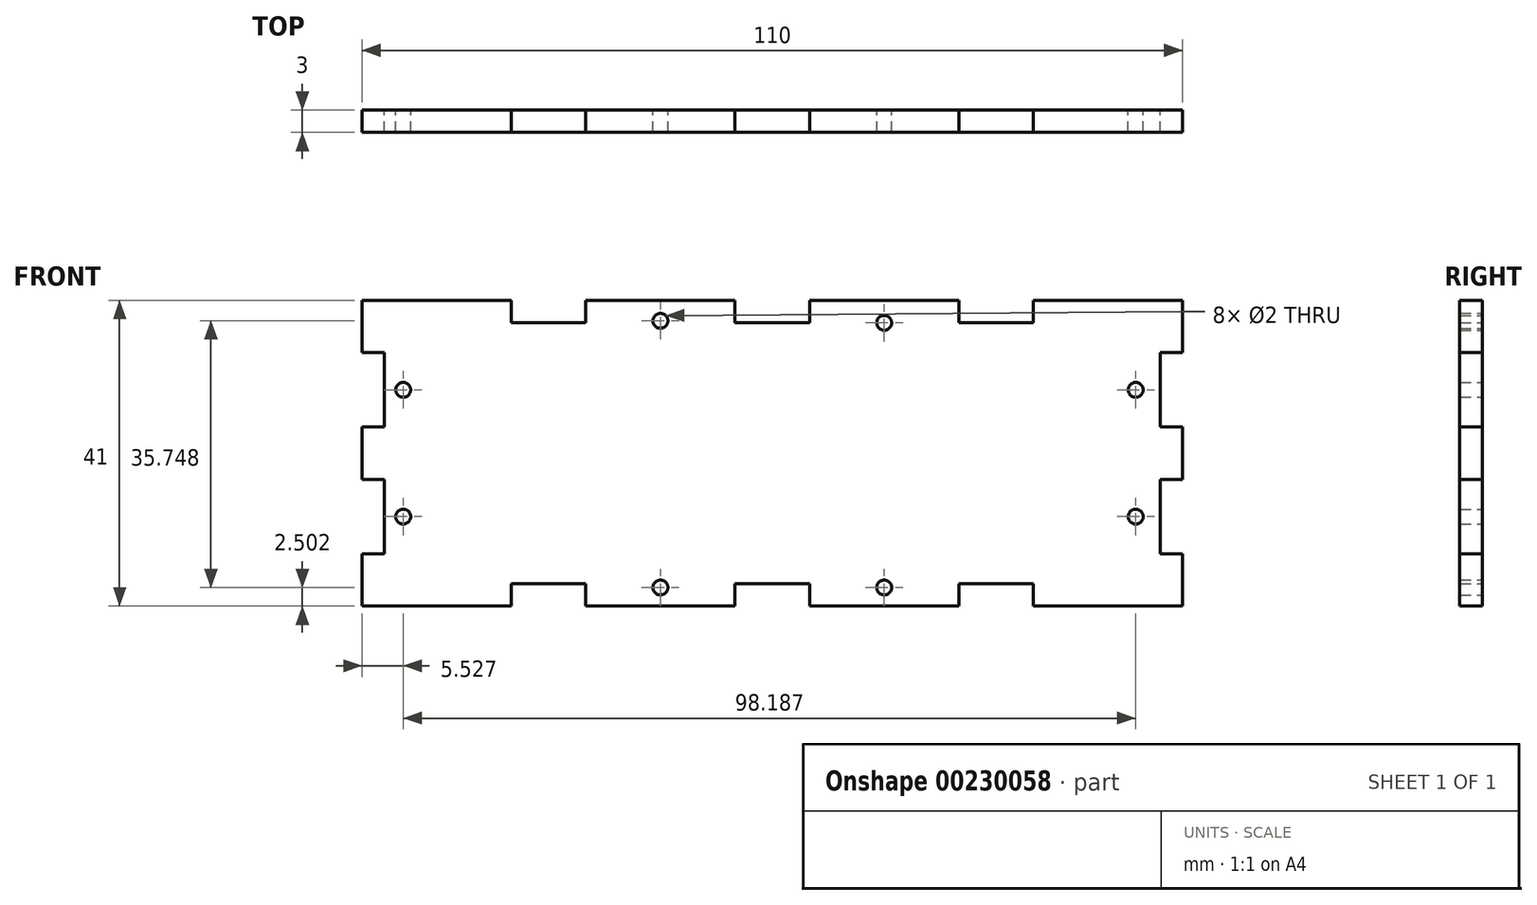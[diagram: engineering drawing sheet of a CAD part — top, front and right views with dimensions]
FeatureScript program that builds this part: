
annotation { "Feature Type Name" : "Feature", "Feature Type Description" : "" }
export const myFeature = defineFeature(function(context is Context, id is Id, definition is map)
    precondition{}
    {
        {
            var Q0;
            Q0=qCreatedBy(makeId("Front.planeOp"),FACE);
            var sketch = newSketch(context, id + "F0", { "sketchPlane" : qUnion([Q0])});
            skLineSegment(sketch, "E0", {"start": v(-54.98, 2.6) * mm, "end": v(-51.98, 2.6) * mm});
            skLineSegment(sketch, "E1", {"start": v(-51.98, 2.6) * mm, "end": v(-51.98, 12.6) * mm});
            skLineSegment(sketch, "E2", {"start": v(-51.98, 12.6) * mm, "end": v(-54.98, 12.6) * mm});
            skLineSegment(sketch, "E3", {"start": v(-54.98, 12.6) * mm, "end": v(-54.98, 19.6) * mm});
            skLineSegment(sketch, "E4", {"start": v(-54.98, 19.6) * mm, "end": v(-34.98, 19.6) * mm});
            skLineSegment(sketch, "E5", {"start": v(-34.98, 19.6) * mm, "end": v(-34.98, 16.6) * mm});
            skLineSegment(sketch, "E6", {"start": v(-34.98, 16.6) * mm, "end": v(-24.98, 16.6) * mm});
            skLineSegment(sketch, "E7", {"start": v(-24.98, 16.6) * mm, "end": v(-24.98, 19.6) * mm});
            skLineSegment(sketch, "E8", {"start": v(-4.98, 19.6) * mm, "end": v(-24.98, 19.6) * mm});
            skLineSegment(sketch, "E9", {"start": v(-4.98, 19.6) * mm, "end": v(-4.98, 16.6) * mm});
            skLineSegment(sketch, "E10", {"start": v(0.02, 16.6) * mm, "end": v(-4.98, 16.6) * mm});
            skCircle(sketch, "E11", {"center": v(-14.98, 16.84) * mm, "radius": 1 * mm});
            skCircle(sketch, "E12", {"center": v(-49.45, 7.6) * mm, "radius": 1 * mm});
            skCircle(sketch, "E13.MirrorC", {"center": v(15.02, 16.57) * mm, "radius": 1 * mm});
            skLineSegment(sketch, "E14", {"start": v(-54.98, 2.6) * mm, "end": v(-54.98, -0.9) * mm});
            skLineSegment(sketch, "E15.MirrorCS", {"start": v(52.02, 12.6) * mm, "end": v(55.02, 12.6) * mm});
            skLineSegment(sketch, "E16.MirrorCS", {"start": v(5.02, 19.6) * mm, "end": v(5.02, 16.6) * mm});
            skLineSegment(sketch, "E17.MirrorCS", {"start": v(35.02, 19.6) * mm, "end": v(35.02, 16.6) * mm});
            skLineSegment(sketch, "E18.MirrorCS", {"start": v(55.02, 2.6) * mm, "end": v(52.02, 2.6) * mm});
            skLineSegment(sketch, "E19.MirrorCS", {"start": v(25.02, 16.6) * mm, "end": v(25.02, 19.6) * mm});
            skCircle(sketch, "E20.MirrorC", {"center": v(48.73, 7.6) * mm, "radius": 1 * mm});
            skLineSegment(sketch, "E21.MirrorCS", {"start": v(55.02, 2.6) * mm, "end": v(55.02, -0.9) * mm});
            skLineSegment(sketch, "E22.MirrorCS", {"start": v(55.02, 12.6) * mm, "end": v(55.02, 19.6) * mm});
            skLineSegment(sketch, "E23.MirrorCS", {"start": v(5.02, 19.6) * mm, "end": v(25.02, 19.6) * mm});
            skLineSegment(sketch, "E24.MirrorCS", {"start": v(35.02, 16.6) * mm, "end": v(25.02, 16.6) * mm});
            skLineSegment(sketch, "E25.MirrorCS", {"start": v(52.02, 2.6) * mm, "end": v(52.02, 12.6) * mm});
            skLineSegment(sketch, "E26.MirrorCS", {"start": v(55.02, 19.6) * mm, "end": v(35.02, 19.6) * mm});
            skLineSegment(sketch, "E27", {"start": v(5.02, 16.6) * mm, "end": v(0.02, 16.6) * mm});
            skLineSegment(sketch, "E28", {"start": v(-54.98, -0.9) * mm, "end": v(55.02, -0.9) * mm, "construction": true});
            skLineSegment(sketch, "E29.MirrorCS", {"start": v(25.02, -18.4) * mm, "end": v(25.02, -21.4) * mm});
            skLineSegment(sketch, "E30.MirrorCS", {"start": v(-4.98, -21.4) * mm, "end": v(-4.98, -18.4) * mm});
            skLineSegment(sketch, "E31.MirrorCS", {"start": v(-54.98, -4.4) * mm, "end": v(-51.98, -4.4) * mm});
            skLineSegment(sketch, "E32.MirrorCS", {"start": v(-34.98, -21.4) * mm, "end": v(-34.98, -18.4) * mm});
            skLineSegment(sketch, "E33.MirrorCS", {"start": v(35.02, -21.4) * mm, "end": v(35.02, -18.4) * mm});
            skLineSegment(sketch, "E34.MirrorCS", {"start": v(-51.98, -14.4) * mm, "end": v(-54.98, -14.4) * mm});
            skLineSegment(sketch, "E35.MirrorCS", {"start": v(5.02, -21.4) * mm, "end": v(5.02, -18.4) * mm});
            skLineSegment(sketch, "E36.MirrorCS", {"start": v(55.02, -4.4) * mm, "end": v(52.02, -4.4) * mm});
            skLineSegment(sketch, "E37.MirrorCS", {"start": v(-24.98, -18.4) * mm, "end": v(-24.98, -21.4) * mm});
            skLineSegment(sketch, "E38.MirrorCS", {"start": v(52.02, -14.4) * mm, "end": v(55.02, -14.4) * mm});
            skCircle(sketch, "E39.MirrorC", {"center": v(-49.45, -9.4) * mm, "radius": 1 * mm});
            skCircle(sketch, "E40.MirrorC", {"center": v(48.73, -9.4) * mm, "radius": 1 * mm});
            skLineSegment(sketch, "E41.MirrorCS", {"start": v(-51.98, -4.4) * mm, "end": v(-51.98, -14.4) * mm});
            skLineSegment(sketch, "E42.MirrorCS", {"start": v(5.02, -18.4) * mm, "end": v(0.02, -18.4) * mm});
            skLineSegment(sketch, "E43.MirrorCS", {"start": v(35.02, -18.4) * mm, "end": v(25.02, -18.4) * mm});
            skLineSegment(sketch, "E44.MirrorCS", {"start": v(55.02, -21.4) * mm, "end": v(35.02, -21.4) * mm});
            skLineSegment(sketch, "E45.MirrorCS", {"start": v(0.02, -18.4) * mm, "end": v(-4.98, -18.4) * mm});
            skLineSegment(sketch, "E46.MirrorCS", {"start": v(-54.98, -14.4) * mm, "end": v(-54.98, -21.4) * mm});
            skLineSegment(sketch, "E47.MirrorCS", {"start": v(-34.98, -18.4) * mm, "end": v(-24.98, -18.4) * mm});
            skLineSegment(sketch, "E48.MirrorCS", {"start": v(55.02, -14.4) * mm, "end": v(55.02, -21.4) * mm});
            skLineSegment(sketch, "E49.MirrorCS", {"start": v(5.02, -21.4) * mm, "end": v(25.02, -21.4) * mm});
            skLineSegment(sketch, "E50.MirrorCS", {"start": v(52.02, -4.4) * mm, "end": v(52.02, -14.4) * mm});
            skLineSegment(sketch, "E51.MirrorCS", {"start": v(-54.98, -21.4) * mm, "end": v(-34.98, -21.4) * mm});
            skLineSegment(sketch, "E52.MirrorCS", {"start": v(-4.98, -21.4) * mm, "end": v(-24.98, -21.4) * mm});
            skLineSegment(sketch, "E53", {"start": v(-54.98, -0.9) * mm, "end": v(-54.98, -4.4) * mm});
            skLineSegment(sketch, "E54", {"start": v(55.02, -0.9) * mm, "end": v(55.02, -4.4) * mm});
            skPoint(sketch, "E55", {"position": v(52.02, 7.6) * mm});
            skPoint(sketch, "E56", {"position": v(15.02, 19.6) * mm});
            skPoint(sketch, "E57", {"position": v(-14.98, 19.6) * mm});
            skPoint(sketch, "E58", {"position": v(-51.98, 7.6) * mm});
            skLineSegment(sketch, "E59", {"start": v(-14.98, 19.6) * mm, "end": v(-14.98, -21.4) * mm, "construction": true});
            skCircle(sketch, "E60", {"center": v(-14.98, -18.9) * mm, "radius": 1 * mm});
            skLineSegment(sketch, "E61", {"start": v(15.02, 19.6) * mm, "end": v(15.02, -21.4) * mm, "construction": true});
            skCircle(sketch, "E62", {"center": v(15.02, -18.9) * mm, "radius": 1 * mm});
            skSolve(sketch);
        }
        {
            var Q0;
            Q0=makeQuery(id+"F0.imprint","IMPRINT",FACE,{"disambiguationData":[TD([[makeQuery(id+"F0.imprint","IMPRINT",EDGE,{"derivedFrom":sQuery(id+"F0.wireOp",EDGE,"E0")}),-1.0]])]});
            extrude(context, id + "F1", {"entities" : qUnion([Q0]), "depth" : 3 * mm});
        }
    });
